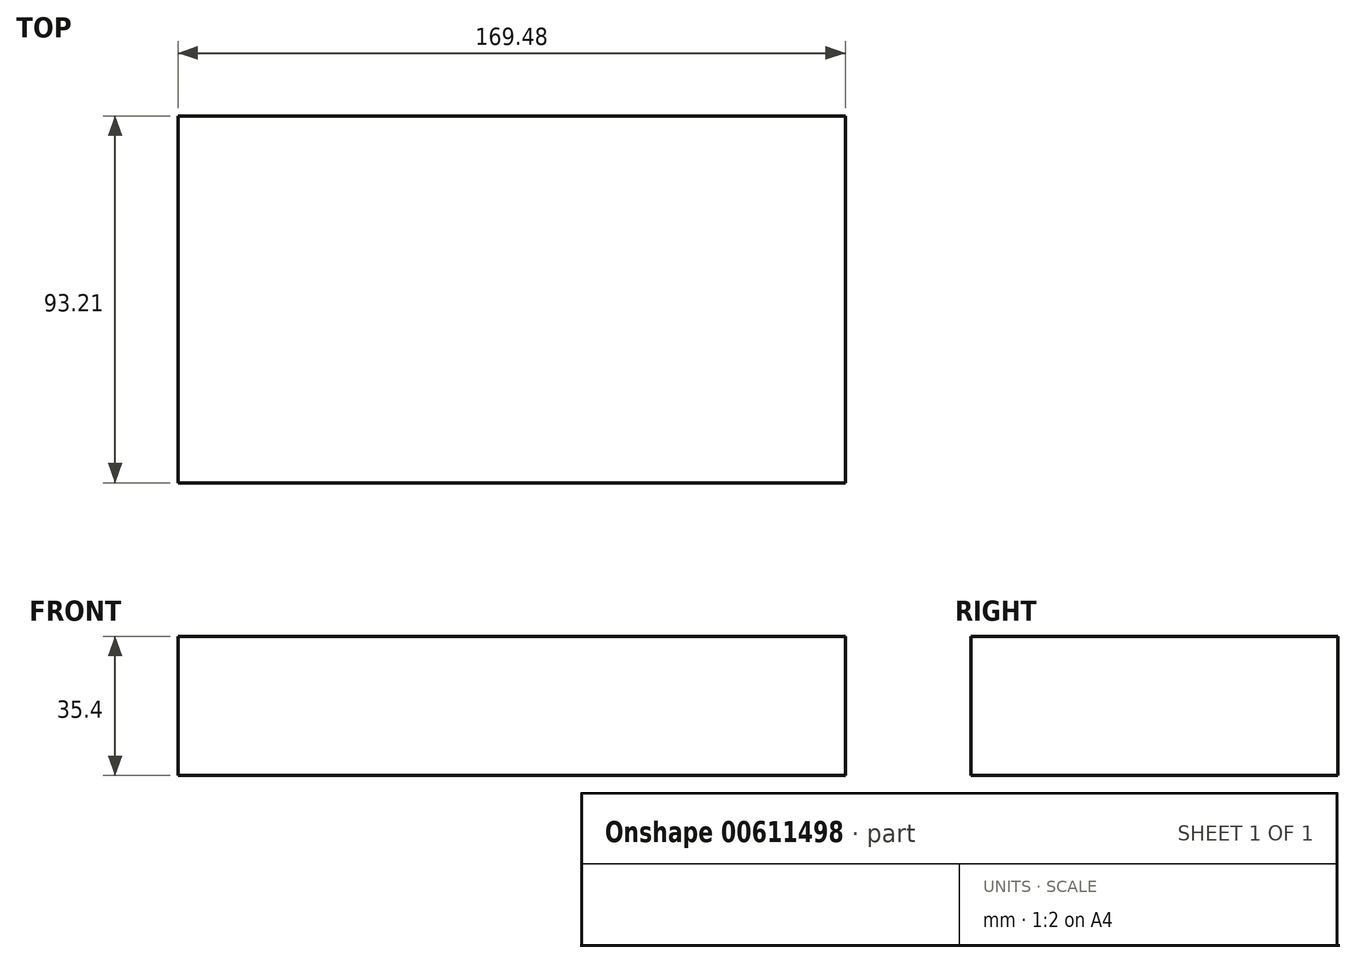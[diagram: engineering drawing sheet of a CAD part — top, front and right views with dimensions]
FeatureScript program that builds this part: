
annotation { "Feature Type Name" : "Feature", "Feature Type Description" : "" }
export const myFeature = defineFeature(function(context is Context, id is Id, definition is map)
    precondition{}
    {
        {
            var Q0;
            Q0=qCreatedBy(makeId("Top.planeOp"),FACE);
            var sketch = newSketch(context, id + "F0", { "sketchPlane" : qUnion([Q0])});
            skLineSegment(sketch, "E0.bottom", {"start": v(79.37, -93.21) * mm, "end": v(15.36, -93.21) * mm});
            skLineSegment(sketch, "E0.top", {"start": v(79.37, 0) * mm, "end": v(15.36, 0) * mm});
            skLineSegment(sketch, "E0.left", {"start": v(79.37, -93.21) * mm, "end": v(79.37, 0) * mm});
            skLineSegment(sketch, "E0.right", {"start": v(15.36, -93.21) * mm, "end": v(15.36, 0) * mm});
            skSolve(sketch);
        }
        {
            var Q0;
            Q0=makeQuery(id+"F0.imprint","IMPRINT",FACE,{"disambiguationData":[TD([[makeQuery(id+"F0.imprint","IMPRINT",EDGE,{"derivedFrom":sQuery(id+"F0.wireOp",EDGE,"E0.bottom")}),-1.0]])]});
            var sketch = newSketch(context, id + "F1", { "sketchPlane" : qUnion([Q0])});
            skSolve(sketch);
        }
        {
            var Q0;
            Q0 = qSketchRegion(id + "F1", true);
            var Q1;
            Q1=makeQuery(id+"F0.imprint","IMPRINT",FACE,{"disambiguationData":[TD([[makeQuery(id+"F0.imprint","IMPRINT",EDGE,{"derivedFrom":sQuery(id+"F0.wireOp",EDGE,"E0.bottom")}),-1.0]])]});
            extrude(context, id + "F2", {"entities" : qUnion([Q0, Q1]), "depth" : 25.4 * mm, "offsetDistance" : 25.4 * mm});
        }
        {
            var Q0;
            Q0=makeQuery(id+"F2.opExtrude","CAP_FACE",FACE,{"disambiguationData":[OSD([sQuery(id+"F0.wireOp",EDGE,"E0.bottom"),sQuery(id+"F0.wireOp",EDGE,"E0.top"),sQuery(id+"F0.wireOp",EDGE,"E0.left"),sQuery(id+"F0.wireOp",EDGE,"E0.right")])],"isStart":false});
            extrude(context, id + "F3", {"entities" : qUnion([Q0]), "operationType" : NewBodyOperationType.ADD, "depth" : 10 * mm, "offsetDistance" : 25 * mm});
        }
        {
            var Q0;
            {var subQ0=sQuery(id+"F0.wireOp",EDGE,"E0.left");Q0=makeQuery(id+"F3.boolean.opBoolean","MERGE",FACE,{"derivedFrom":[makeQuery(id+"F2.opExtrude","SWEPT_FACE",FACE,{"disambiguationData":[OSD([subQ0])]}),makeQuery(id+"F3.opExtrude","SWEPT_FACE",FACE,{"disambiguationData":[OSD([subQ0])]})]});}
            extrude(context, id + "F4", {"entities" : qUnion([Q0]), "operationType" : NewBodyOperationType.ADD, "depth" : 74.66 * mm, "offsetDistance" : 25 * mm});
        }
        {
            var Q0;
            Q0=makeQuery(id+"F4.opExtrude","CAP_FACE",FACE,{"disambiguationData":[OSD([sQuery(id+"F0.wireOp",EDGE,"E0.left")])],"isStart":false});
            extrude(context, id + "F5", {"entities" : qUnion([Q0]), "operationType" : NewBodyOperationType.ADD, "depth" : 30.8 * mm, "offsetDistance" : 25 * mm});
        }
    });
